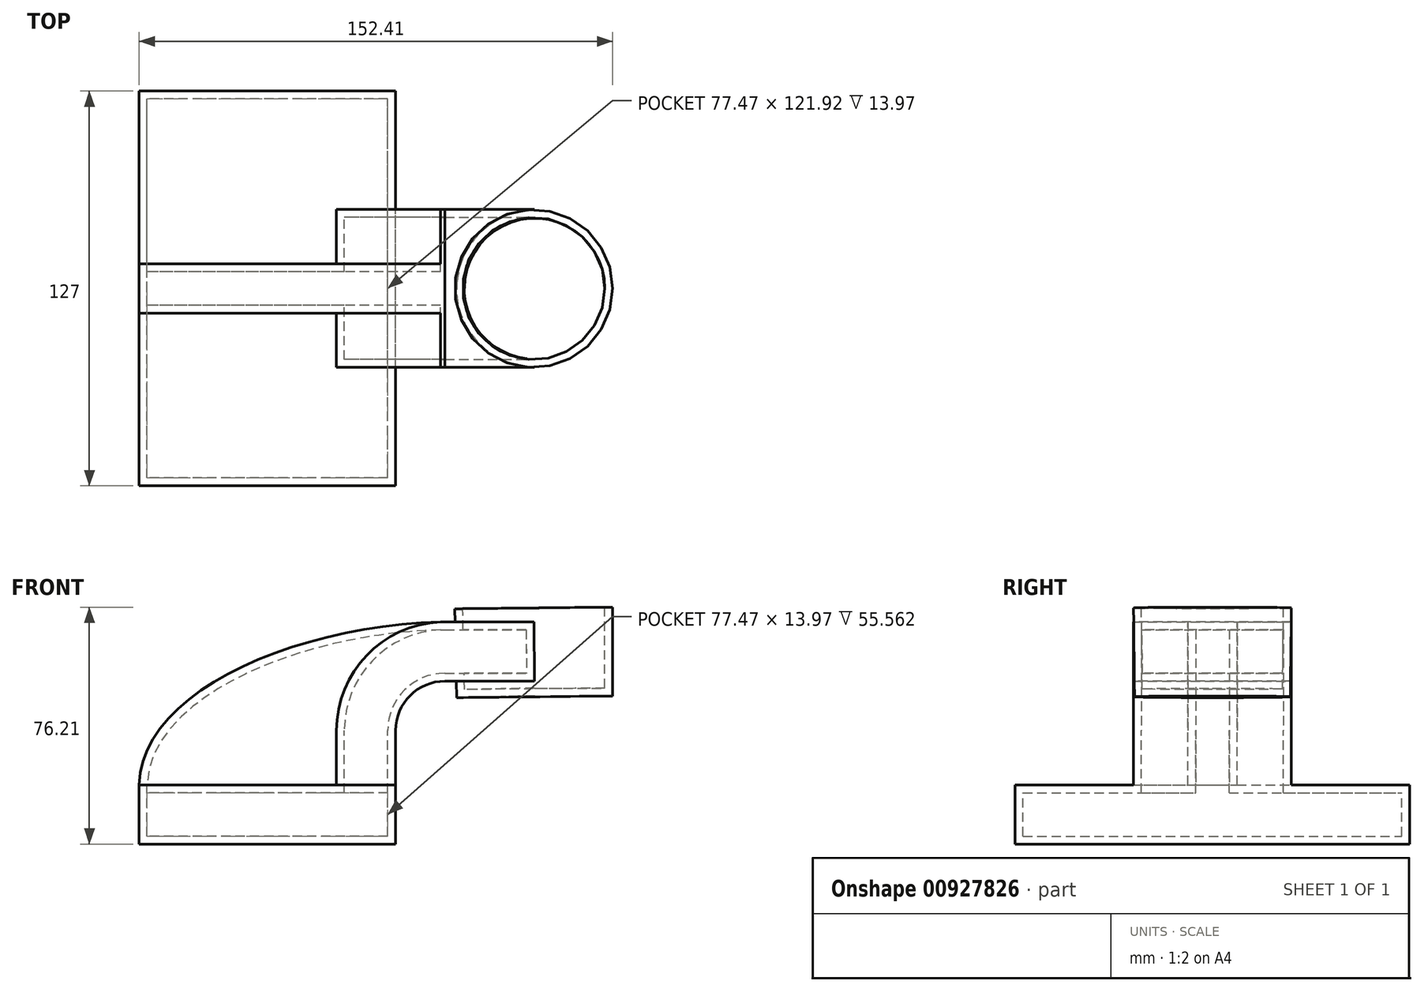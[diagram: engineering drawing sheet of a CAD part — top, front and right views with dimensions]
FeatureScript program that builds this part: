
annotation { "Feature Type Name" : "Feature", "Feature Type Description" : "" }
export const myFeature = defineFeature(function(context is Context, id is Id, definition is map)
    precondition{}
    {
        {
            var Q0;
            Q0=qCreatedBy(makeId("Front.planeOp"),FACE);
            var sketch = newSketch(context, id + "F0", { "sketchPlane" : qUnion([Q0])});
            skLineSegment(sketch, "E0.bottom", {"start": v(41.28, -9.52) * mm, "end": v(-41.28, -9.53) * mm});
            skLineSegment(sketch, "E0.top", {"start": v(41.28, 9.53) * mm, "end": v(-41.28, 9.53) * mm});
            skLineSegment(sketch, "E0.left", {"start": v(41.28, -9.52) * mm, "end": v(41.28, 9.53) * mm});
            skLineSegment(sketch, "E0.right", {"start": v(-41.28, -9.53) * mm, "end": v(-41.28, 9.53) * mm});
            skPoint(sketch, "E0.middle", {"position": v(0, 0) * mm});
            skLineSegment(sketch, "E1.bottom", {"start": v(111.12, 38.1) * mm, "end": v(60.32, 38.1) * mm});
            skLineSegment(sketch, "E1.top", {"start": v(111.12, 66.67) * mm, "end": v(60.32, 66.67) * mm});
            skLineSegment(sketch, "E1.left", {"start": v(111.12, 38.1) * mm, "end": v(111.12, 66.68) * mm});
            skLineSegment(sketch, "E1.right", {"start": v(60.32, 38.1) * mm, "end": v(60.32, 66.67) * mm});
            skPoint(sketch, "E1.middle", {"position": v(85.72, 52.39) * mm});
            skLineSegment(sketch, "E2", {"start": v(41.28, 9.53) * mm, "end": v(41.28, 27) * mm});
            skArc(sketch, "E3", {"start": v(41.27, 27) * mm, "mid": v(45.92, 38.23) * mm, "end": v(57.15, 42.88) * mm});
            skLineSegment(sketch, "E4", {"start": v(57.15, 42.88) * mm, "end": v(86.02, 42.88) * mm});
            skLineSegment(sketch, "E5.0", {"start": v(57.15, 61.93) * mm, "end": v(86.02, 61.93) * mm});
            skArc(sketch, "E5.1", {"start": v(22.23, 27) * mm, "mid": v(32.45, 51.7) * mm, "end": v(57.15, 61.93) * mm});
            skLineSegment(sketch, "E5.2", {"start": v(22.22, 9.53) * mm, "end": v(22.22, 27) * mm});
            skLineSegment(sketch, "E6", {"start": v(85.72, 66.67) * mm, "end": v(86.02, 38.1) * mm});
            skFitSpline(sketch, "E7", {"points": [v(-41.28, 9.53) * mm, v(57.15, 61.93) * mm], "startDerivative": vector(1.88, 90.16) * mm, "endDerivative": vector(143.46, 2.41) * mm});
            skSolve(sketch);
        }
        {
            var Q0;
            Q0=makeQuery(id+"F0.imprint","IMPRINT",FACE,{"disambiguationData":[TD([[makeQuery(id+"F0.imprint","IMPRINT",EDGE,{"derivedFrom":sQuery(id+"F0.wireOp",EDGE,"E0.bottom")}),-1.0]])]});
            extrude(context, id + "F1", {"entities" : qUnion([Q0]), "endBound" : BoundingType.SYMMETRIC, "depth" : 127 * mm, "offsetDistance" : 25.4 * mm});
        }
        {
            var Q0;
            {var subQ1=sQuery(id+"F0.wireOp",EDGE,"E2");Q0=makeQuery(id+"F0.imprint","IMPRINT",FACE,{"disambiguationData":[TD([[makeQuery(id+"F0.imprint","IMPRINT",EDGE,{"derivedFrom":subQ1}),1.0]])]});}
            var Q1;
            {var subQ0=sQuery(id+"F0.wireOp",EDGE,"E4");var subQ1=sQuery(id+"F0.wireOp",EDGE,"E1.right");var subQ2=makeQuery(id+"F0.imprint","INTERSECT",VERTEX,{"derivedFrom":[subQ1,subQ0]});Q1=makeQuery(id+"F0.imprint","IMPRINT",FACE,{"disambiguationData":[TD([[makeQuery(id+"F0.imprint","IMPRINT",EDGE,{"disambiguationData":[TD([[subQ2,-1.0]])],"derivedFrom":subQ1}),-1.0]])]});}
            extrude(context, id + "F2", {"entities" : qUnion([Q0, Q1]), "operationType" : NewBodyOperationType.ADD, "endBound" : BoundingType.SYMMETRIC, "depth" : 50.8 * mm, "offsetDistance" : 25.4 * mm});
        }
        {
            var Q0;
            {var subQ3=sQuery(id+"F0.wireOp",EDGE,"E5.2");Q0=makeQuery(id+"F0.imprint","IMPRINT",FACE,{"disambiguationData":[TD([[makeQuery(id+"F0.imprint","IMPRINT",EDGE,{"derivedFrom":subQ3}),1.0]])]});}
            extrude(context, id + "F3", {"entities" : qUnion([Q0]), "operationType" : NewBodyOperationType.ADD, "endBound" : BoundingType.SYMMETRIC, "depth" : 15.88 * mm, "offsetDistance" : 25.4 * mm});
        }
        {
            var Q0;
            {var subQ0=sQuery(id+"F0.wireOp",EDGE,"E1.left");Q0=makeQuery(id+"F0.imprint","IMPRINT",FACE,{"disambiguationData":[TD([[makeQuery(id+"F0.imprint","IMPRINT",EDGE,{"derivedFrom":subQ0}),1.0]])]});}
            var Q1;
            Q1=sQuery(id+"F0.wireOp",EDGE,"E6");
            revolve(context, id + "F4", {"operationType" : NewBodyOperationType.ADD, "surfaceOperationType" : NewSurfaceOperationType.NEW, "entities" : qUnion([Q0]), "axis" : qUnion([Q1]), "revolveType" : RevolveType.FULL});
        }
        {
            var Q0;
            Q0=makeQuery(id+"F4.opRevolve","SWEPT_FACE",FACE,{"disambiguationData":[OSD([sQuery(id+"F0.wireOp",EDGE,"E1.top")])]});
            shell(context, id + "F5", {"entities" : qUnion([Q0]), "thickness" : 2.54 * mm});
        }
    });
